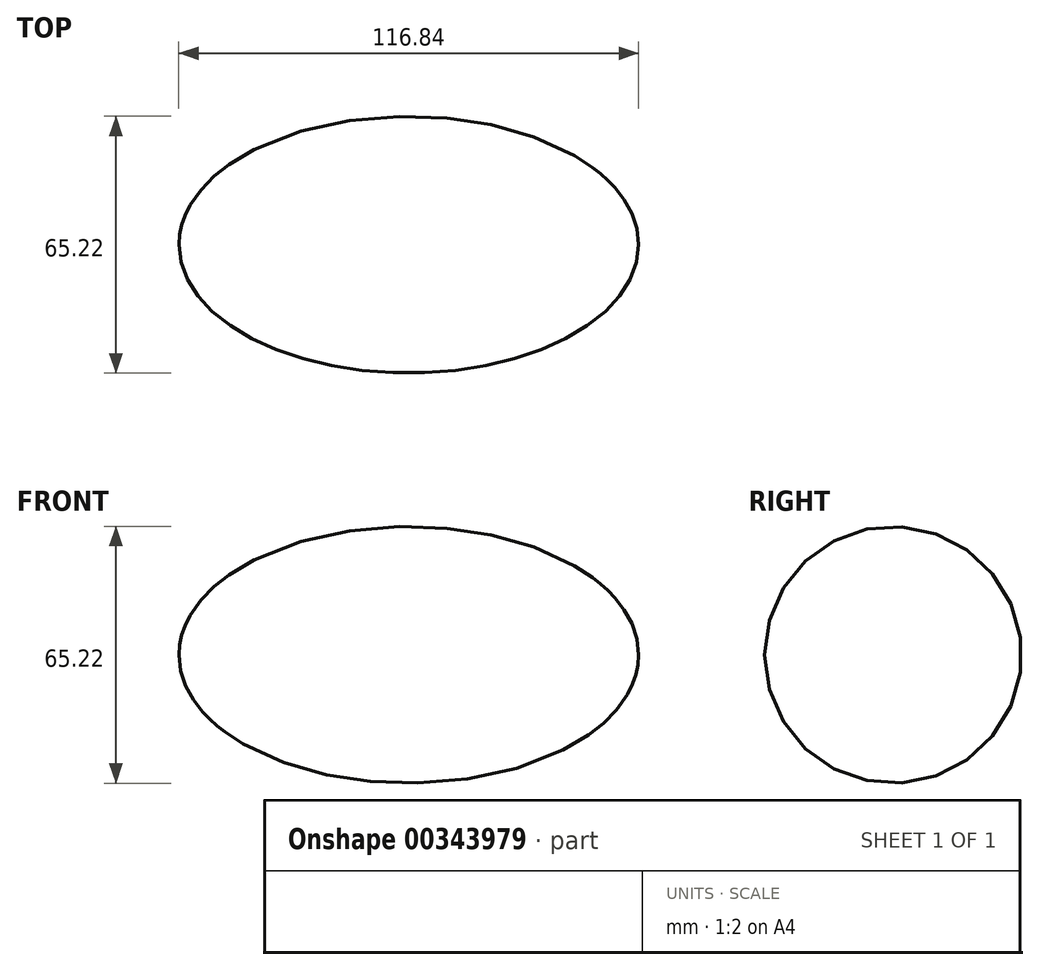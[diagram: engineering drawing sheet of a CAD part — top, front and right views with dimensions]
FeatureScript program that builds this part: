
annotation { "Feature Type Name" : "Feature", "Feature Type Description" : "" }
export const myFeature = defineFeature(function(context is Context, id is Id, definition is map)
    precondition{}
    {
        {
            var Q0;
            Q0=qCreatedBy(makeId("Top.planeOp"),FACE);
            var sketch = newSketch(context, id + "F0", { "sketchPlane" : qUnion([Q0])});
            skEllipse(sketch, "E0", {"center": v(0, 0) * mm, "majorRadius": 58.42 * mm, "minorRadius": 32.61 * mm, "majorAxis": v(-1, 0)});
            skLineSegment(sketch, "E1", {"start": v(-58.42, 0) * mm, "end": v(58.42, 0) * mm});
            skSolve(sketch);
        }
        {
            var Q0;
            {var subQ0=sQuery(id+"F0.wireOp",EDGE,"E1");Q0=makeQuery(id+"F0.imprint","IMPRINT",FACE,{"disambiguationData":[TD([[makeQuery(id+"F0.imprint","IMPRINT",EDGE,{"derivedFrom":subQ0}),-1.0]])]});}
            var Q1;
            Q1=sQuery(id+"F0.wireOp",EDGE,"E0");
            var Q2;
            Q2=sQuery(id+"F0.wireOp",EDGE,"E1");
            revolve(context, id + "F1", {"entities" : qUnion([Q0]), "surfaceEntities" : qUnion([Q1]), "axis" : qUnion([Q2]), "revolveType" : RevolveType.FULL});
        }
    });
